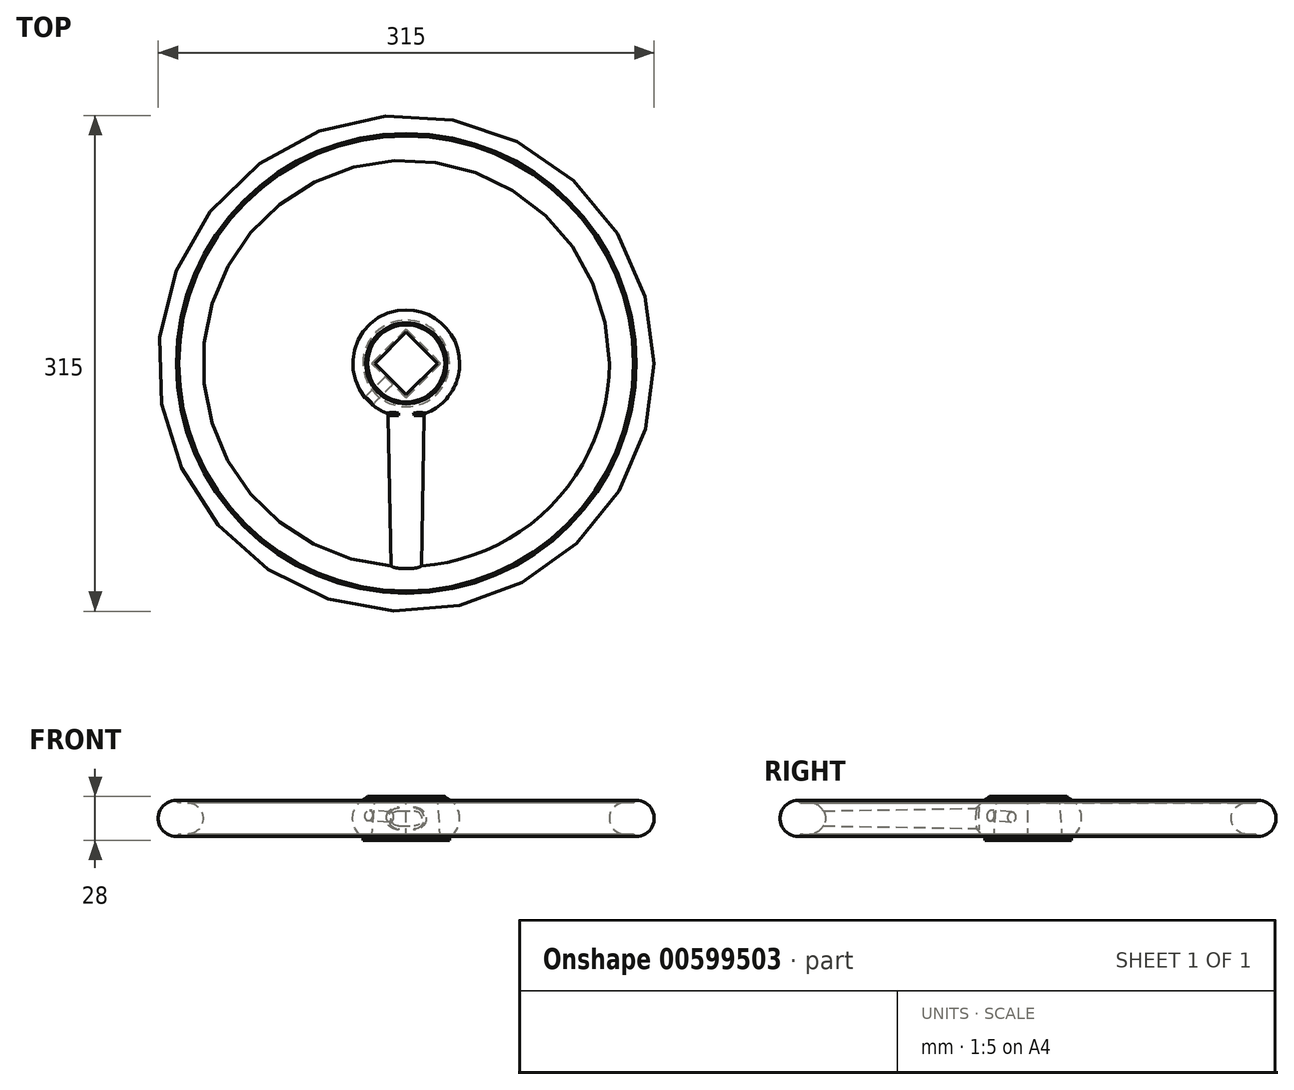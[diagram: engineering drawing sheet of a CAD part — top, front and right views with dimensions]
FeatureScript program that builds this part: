
annotation { "Feature Type Name" : "Feature", "Feature Type Description" : "" }
export const myFeature = defineFeature(function(context is Context, id is Id, definition is map)
    precondition{}
    {
        {
            var Q0;
            Q0=qCreatedBy(makeId("Front.planeOp"),FACE);
            var sketch = newSketch(context, id + "F0", { "sketchPlane" : qUnion([Q0])});
            skLineSegment(sketch, "E0", {"start": v(0, 50.45) * mm, "end": v(0, 0) * mm, "construction": true});
            skLineSegment(sketch, "E1", {"start": v(0, 0) * mm, "end": v(-146, 0) * mm, "construction": true});
            skLineSegment(sketch, "E2.bottom", {"start": v(0, 14) * mm, "end": v(-27.5, 14) * mm});
            skLineSegment(sketch, "E2.top", {"start": v(0, -14) * mm, "end": v(-27.5, -14) * mm});
            skLineSegment(sketch, "E2.left", {"start": v(0, 14) * mm, "end": v(0, -14) * mm});
            skLineSegment(sketch, "E2.right", {"start": v(-27.5, 14) * mm, "end": v(-27.5, 11.82) * mm});
            skLineSegment(sketch, "E3", {"start": v(0, 0) * mm, "end": v(-20, 0) * mm, "construction": true});
            skArc(sketch, "E4", {"start": v(-27.5, 11.82) * mm, "mid": v(-34, 0) * mm, "end": v(-27.5, -11.82) * mm});
            skLineSegment(sketch, "E5.trimOffspring", {"start": v(-27.5, -11.82) * mm, "end": v(-27.5, -14) * mm});
            skArc(sketch, "E6", {"start": v(-146, 11.5) * mm, "mid": v(-157.5, 0) * mm, "end": v(-146, -11.5) * mm});
            skArc(sketch, "E7", {"start": v(-139, 10) * mm, "mid": v(-129, 0) * mm, "end": v(-139, -10) * mm});
            skLineSegment(sketch, "E8", {"start": v(-146, 11.5) * mm, "end": v(-146, -11.5) * mm, "construction": true});
            skLineSegment(sketch, "E9", {"start": v(-139, 10) * mm, "end": v(-144.5, 10) * mm});
            skLineSegment(sketch, "E10", {"start": v(-144.5, 10) * mm, "end": v(-146, 11.5) * mm});
            skLineSegment(sketch, "E11.MirrorCS", {"start": v(-144.5, -10) * mm, "end": v(-146, -11.5) * mm});
            skLineSegment(sketch, "E12.MirrorCS", {"start": v(-139, -10) * mm, "end": v(-144.5, -10) * mm});
            skPoint(sketch, "E13", {"position": v(-157.5, 0) * mm});
            skLineSegment(sketch, "E14", {"start": v(-139, 10) * mm, "end": v(-139, 0) * mm, "construction": true});
            skSolve(sketch);
        }
        {
            var Q0;
            Q0 = qSketchRegion(id + "F0", true);
            var Q1;
            Q1=sQuery(id+"F0.wireOp",EDGE,"E0");
            revolve(context, id + "F1", {"entities" : qUnion([Q0]), "axis" : qUnion([Q1]), "revolveType" : RevolveType.FULL});
        }
        {
            var Q0;
            Q0=qCreatedBy(makeId("Front.planeOp"),FACE);
            var sketch = newSketch(context, id + "F2", { "sketchPlane" : qUnion([Q0])});
            skLineSegment(sketch, "E15", {"start": v(5, 0) * mm, "end": v(-5, 0) * mm, "construction": true});
            skArc(sketch, "E16", {"start": v(5, -7) * mm, "mid": v(12, 0) * mm, "end": v(5, 7) * mm});
            skArc(sketch, "E17", {"start": v(-5, 7) * mm, "mid": v(-12, 0) * mm, "end": v(-5, -7) * mm});
            skLineSegment(sketch, "E18", {"start": v(5, 7) * mm, "end": v(-5, 7) * mm});
            skLineSegment(sketch, "E19.MirrorCS", {"start": v(5, -7) * mm, "end": v(-5, -7) * mm});
            skSolve(sketch);
        }
        {
            var Q0;
            Q0 = qSketchRegion(id + "F2", true);
            var Q1;
            Q1=makeQuery(id+"F1.opRevolve","SWEPT_FACE",FACE,{"disambiguationData":[OSD([sQuery(id+"F0.wireOp",EDGE,"E7")])]});
            extrude(context, id + "F3", {"entities" : qUnion([Q0]), "endBound" : BoundingType.UP_TO_SURFACE, "depth" : 25 * mm, "endBoundEntityFace" : qUnion([Q1]), "offsetDistance" : 25 * mm, "hasDraft" : true, "draftAngle" : 1 * degree, "draftPullDirection" : true});
        }
        {
            var Q0;
            Q0=makeQuery(id+"F1.opRevolve","SWEPT_BODY",BODY,{"disambiguationData":[OSD([sQuery(id+"F0.wireOp",EDGE,"E6"),sQuery(id+"F0.wireOp",EDGE,"E7"),sQuery(id+"F0.wireOp",EDGE,"E9"),sQuery(id+"F0.wireOp",EDGE,"E10"),sQuery(id+"F0.wireOp",EDGE,"E11.MirrorCS"),sQuery(id+"F0.wireOp",EDGE,"E12.MirrorCS")])]});
            var Q1;
            Q1=makeQuery(id+"F8h7LBErxSmQ6eF_3.2.F3.opExtrude","SWEPT_BODY",BODY,{"disambiguationData":[OSD([sQuery(id+"F2.wireOp",EDGE,"E16"),sQuery(id+"F2.wireOp",EDGE,"E17"),sQuery(id+"F2.wireOp",EDGE,"E18"),sQuery(id+"F2.wireOp",EDGE,"E19.MirrorCS")])]});
            var Q2;
            Q2=makeQuery(id+"F8h7LBErxSmQ6eF_3.3.F3.opExtrude","SWEPT_BODY",BODY,{"disambiguationData":[OSD([sQuery(id+"F2.wireOp",EDGE,"E16"),sQuery(id+"F2.wireOp",EDGE,"E17"),sQuery(id+"F2.wireOp",EDGE,"E18"),sQuery(id+"F2.wireOp",EDGE,"E19.MirrorCS")])]});
            var Q3;
            Q3=makeQuery(id+"F3.opExtrude","SWEPT_BODY",BODY,{"disambiguationData":[OSD([sQuery(id+"F2.wireOp",EDGE,"E16"),sQuery(id+"F2.wireOp",EDGE,"E17"),sQuery(id+"F2.wireOp",EDGE,"E18"),sQuery(id+"F2.wireOp",EDGE,"E19.MirrorCS")])]});
            var Q4;
            Q4=makeQuery(id+"F8h7LBErxSmQ6eF_3.1.F3.opExtrude","SWEPT_BODY",BODY,{"disambiguationData":[OSD([sQuery(id+"F2.wireOp",EDGE,"E16"),sQuery(id+"F2.wireOp",EDGE,"E17"),sQuery(id+"F2.wireOp",EDGE,"E18"),sQuery(id+"F2.wireOp",EDGE,"E19.MirrorCS")])]});
            var Q5;
            Q5=makeQuery(id+"F1.opRevolve","SWEPT_BODY",BODY,{"disambiguationData":[OSD([sQuery(id+"F0.wireOp",EDGE,"E2.bottom"),sQuery(id+"F0.wireOp",EDGE,"E2.top"),sQuery(id+"F0.wireOp",EDGE,"E2.left"),sQuery(id+"F0.wireOp",EDGE,"E2.right"),sQuery(id+"F0.wireOp",EDGE,"E4"),sQuery(id+"F0.wireOp",EDGE,"E5.trimOffspring")])]});
            booleanBodies(context, id + "F4", {"operationType" : BooleanOperationType.UNION, "tools" : qUnion([Q0, Q1, Q2, Q3, Q4, Q5])});
        }
        {
            var Q0;
            Q0=makeQuery(id+"F3.opExtrude","CAP_EDGE",EDGE,{"disambiguationData":[OSD([sQuery(id+"F2.wireOp",EDGE,"E18")])],"isStart":false});
            var Q1;
            Q1=makeQuery(id+"F4.opBoolean","INTERSECT",EDGE,{"derivedFrom":[makeQuery(id+"F1.opRevolve","SWEPT_FACE",FACE,{"disambiguationData":[OSD([sQuery(id+"F0.wireOp",EDGE,"E4")])]}),makeQuery(id+"F3.opExtrude","SWEPT_FACE",FACE,{"disambiguationData":[OSD([sQuery(id+"F2.wireOp",EDGE,"E18")])]})]});
            var Q2;
            Q2=makeQuery(id+"F8h7LBErxSmQ6eF_3.2.F3.opExtrude","CAP_EDGE",EDGE,{"disambiguationData":[OSD([sQuery(id+"F2.wireOp",EDGE,"E18")])],"isStart":false});
            var Q3;
            Q3=makeQuery(id+"F8h7LBErxSmQ6eF_3.1.F3.opExtrude","CAP_EDGE",EDGE,{"disambiguationData":[OSD([sQuery(id+"F2.wireOp",EDGE,"E18")])],"isStart":false});
            var Q4;
            Q4=makeQuery(id+"F8h7LBErxSmQ6eF_3.3.F3.opExtrude","CAP_EDGE",EDGE,{"disambiguationData":[OSD([sQuery(id+"F2.wireOp",EDGE,"E18")])],"isStart":false});
            var Q5;
            Q5=makeQuery(id+"F4.opBoolean","INTERSECT",EDGE,{"derivedFrom":[makeQuery(id+"F1.opRevolve","SWEPT_FACE",FACE,{"disambiguationData":[OSD([sQuery(id+"F0.wireOp",EDGE,"E4")])]}),makeQuery(id+"F8h7LBErxSmQ6eF_3.2.F3.opExtrude","SWEPT_FACE",FACE,{"disambiguationData":[OSD([sQuery(id+"F2.wireOp",EDGE,"E18")])]})]});
            var Q6;
            Q6=makeQuery(id+"F4.opBoolean","INTERSECT",EDGE,{"derivedFrom":[makeQuery(id+"F1.opRevolve","SWEPT_FACE",FACE,{"disambiguationData":[OSD([sQuery(id+"F0.wireOp",EDGE,"E4")])]}),makeQuery(id+"F8h7LBErxSmQ6eF_3.1.F3.opExtrude","SWEPT_FACE",FACE,{"disambiguationData":[OSD([sQuery(id+"F2.wireOp",EDGE,"E18")])]})]});
            var Q7;
            Q7=makeQuery(id+"F4.opBoolean","INTERSECT",EDGE,{"derivedFrom":[makeQuery(id+"F1.opRevolve","SWEPT_FACE",FACE,{"disambiguationData":[OSD([sQuery(id+"F0.wireOp",EDGE,"E4")])]}),makeQuery(id+"F8h7LBErxSmQ6eF_3.3.F3.opExtrude","SWEPT_FACE",FACE,{"disambiguationData":[OSD([sQuery(id+"F2.wireOp",EDGE,"E18")])]})]});
            fillet(context, id + "F5", {"entities" : qUnion([Q0, Q1, Q2, Q3, Q4, Q5, Q6, Q7]), "radius" : 2 * mm, "tangentPropagation" : true, "allowEdgeOverflow" : false});
        }
        {
            var Q0;
            Q0=makeQuery(id+"F1.opRevolve","SWEPT_FACE",FACE,{"disambiguationData":[OSD([sQuery(id+"F0.wireOp",EDGE,"E2.bottom")])]});
            var sketch = newSketch(context, id + "F6", { "sketchPlane" : qUnion([Q0])});
            skCircle(sketch, "E20.cCircle", {"center": v(0, 0) * mm, "radius": 14 * mm, "construction": true});
            skLineSegment(sketch, "E20.0", {"start": v(-19.8, 0) * mm, "end": v(0, 19.8) * mm});
            skLineSegment(sketch, "E20.1", {"start": v(0, 19.8) * mm, "end": v(19.8, 0) * mm});
            skLineSegment(sketch, "E20.2", {"start": v(19.8, 0) * mm, "end": v(0, -19.8) * mm});
            skLineSegment(sketch, "E20.3", {"start": v(0, -19.8) * mm, "end": v(-19.8, 0) * mm});
            skPoint(sketch, "E20.0.midPoint", {"position": v(-9.9, 9.9) * mm});
            skLineSegment(sketch, "E21", {"start": v(0, 19.8) * mm, "end": v(0, -19.8) * mm, "construction": true});
            skSolve(sketch);
        }
        {
            var Q0;
            Q0 = qSketchRegion(id + "F6", true);
            extrude(context, id + "F7", {"entities" : qUnion([Q0]), "operationType" : NewBodyOperationType.REMOVE, "endBound" : BoundingType.THROUGH_ALL, "oppositeDirection" : true, "depth" : 25 * mm, "offsetDistance" : 25 * mm, "hasDraft" : true, "draftAngle" : 3 * degree});
        }
        {
            var Q0;
            Q0=makeQuery(id+"F1.opRevolve","SWEPT_EDGE",EDGE,{"disambiguationData":[OSD([sQuery(id+"F0.wireOp",EDGE,"E2.bottom"),sQuery(id+"F0.wireOp",EDGE,"E2.right")])]});
            chamfer(context, id + "F8", {"entities" : qUnion([Q0]), "width" : 3 * mm, "tangentPropagation" : true});
        }
        {
            var Q0;
            Q0=makeQuery(id+"F7.boolean.opBoolean","COPY",FACE,{"derivedFrom":makeQuery(id+"F7.opExtrude","SWEPT_FACE",FACE,{"disambiguationData":[OSD([sQuery(id+"F6.wireOp",EDGE,"E20.3")])]})});
            var sketch = newSketch(context, id + "F9", { "sketchPlane" : qUnion([Q0])});
            skPoint(sketch, "E22", {"position": v(0, 0) * mm});
            skSolve(sketch);
        }
        {
            var Q0;
            Q0=sQuery(id+"F9.wireOp",VERTEX,"E22");
            var Q1;
            Q1=makeQuery(id+"F1.opRevolve","SWEPT_BODY",BODY,{"disambiguationData":[OSD([sQuery(id+"F0.wireOp",EDGE,"E6"),sQuery(id+"F0.wireOp",EDGE,"E7"),sQuery(id+"F0.wireOp",EDGE,"E9"),sQuery(id+"F0.wireOp",EDGE,"E10"),sQuery(id+"F0.wireOp",EDGE,"E11.MirrorCS"),sQuery(id+"F0.wireOp",EDGE,"E12.MirrorCS")])]});
            hole(context, id + "F10", {"style" : HoleStyle.SIMPLE, "endStyle" : HoleEndStyle.BLIND, "standardTappedOrClearance" : lookupTablePath({ "standard" : "ISO", "engagement" : "75%", "pitch" : "1.25 mm", "size" : "M8", "type" : "Tapped" }), "standardBlindInLast" : lookupTablePath({ "standard" : "ISO", "engagement" : "75%", "pitch" : "1.25 mm", "size" : "M8", "type" : "Tapped" }), "holeDiameter" : 6.8 * mm, "majorDiameter" : 8 * mm, "showTappedDepth" : true, "holeDepth" : 22.25 * mm, "tappedDepth" : 18.5 * mm, "tapClearance" : 3, "startFromSketch" : true, "locations" : qUnion([Q0]), "scope" : qUnion([Q1])});
        }
    });
